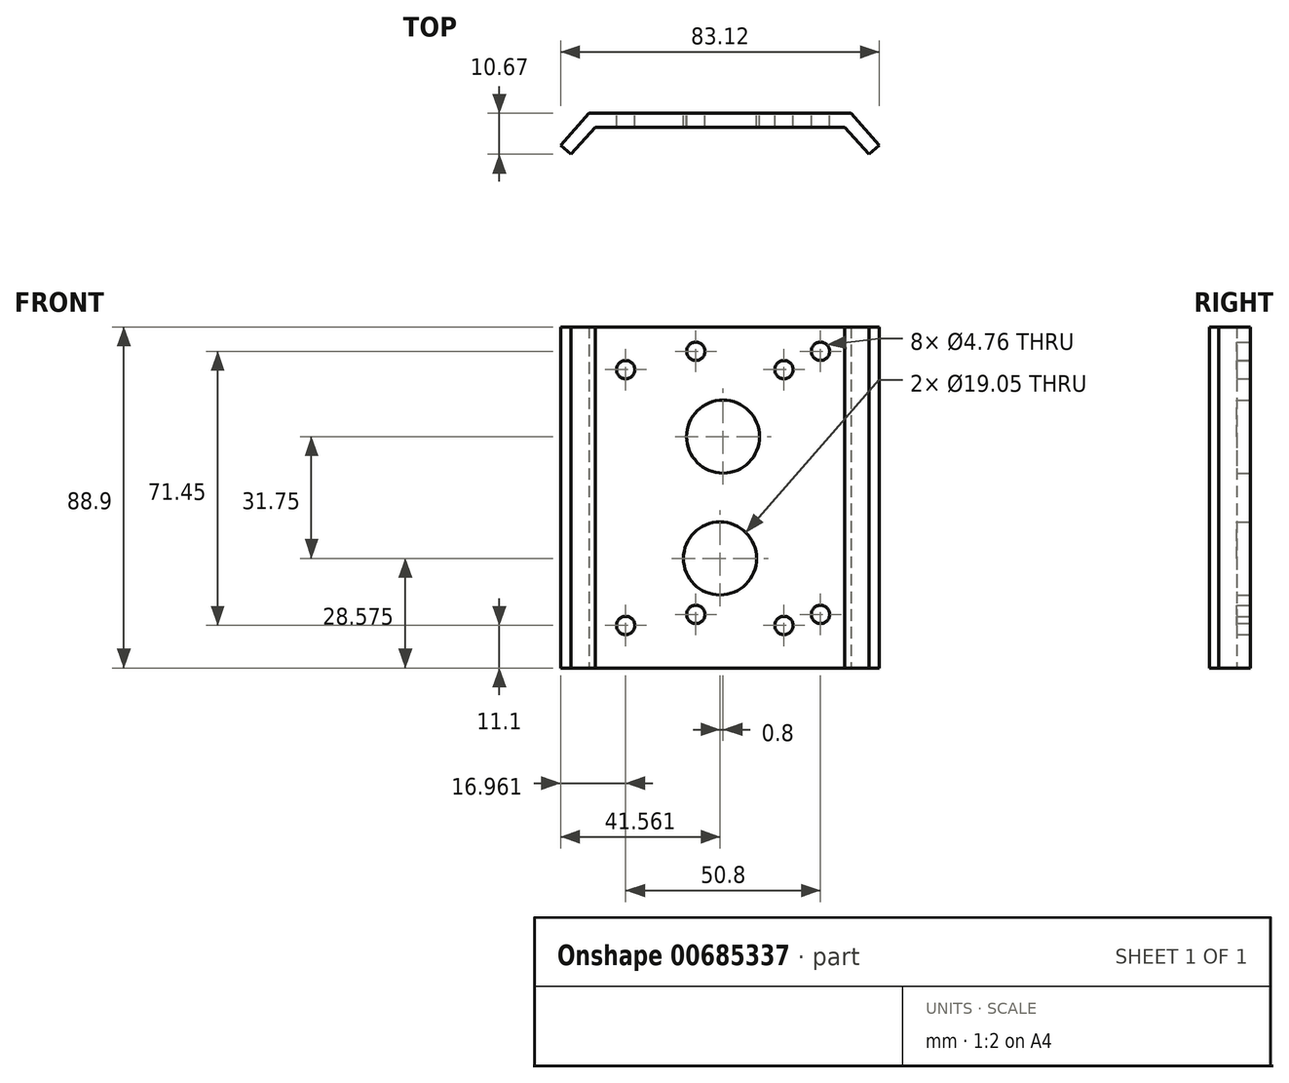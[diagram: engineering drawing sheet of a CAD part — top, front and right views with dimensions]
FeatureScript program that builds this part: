
annotation { "Feature Type Name" : "Feature", "Feature Type Description" : "" }
export const myFeature = defineFeature(function(context is Context, id is Id, definition is map)
    precondition{}
    {
        {
            var Q0;
            Q0=qCreatedBy(makeId("Top.planeOp"),FACE);
            var sketch = newSketch(context, id + "F0", { "sketchPlane" : qUnion([Q0])});
            skLineSegment(sketch, "E0", {"start": v(-57.76, 10.67) * mm, "end": v(10.54, 10.67) * mm});
            skLineSegment(sketch, "E1", {"start": v(10.54, 10.67) * mm, "end": v(17.95, 2.38) * mm});
            skLineSegment(sketch, "E2", {"start": v(15.3, 0) * mm, "end": v(8.94, 7.1) * mm});
            skLineSegment(sketch, "E3", {"start": v(8.94, 7.1) * mm, "end": v(-56.15, 7.1) * mm});
            skLineSegment(sketch, "E4", {"start": v(-56.15, 7.1) * mm, "end": v(-62.5, 0) * mm});
            skLineSegment(sketch, "E5", {"start": v(15.3, 0) * mm, "end": v(17.95, 2.38) * mm});
            skLineSegment(sketch, "E6", {"start": v(-62.5, 0) * mm, "end": v(-65.17, 2.39) * mm});
            skLineSegment(sketch, "E7", {"start": v(-65.17, 2.39) * mm, "end": v(-57.76, 10.67) * mm});
            skLineSegment(sketch, "E8", {"start": v(-63.83, 1.2) * mm, "end": v(-52.04, 14.38) * mm, "construction": true});
            skLineSegment(sketch, "E9", {"start": v(16.62, 1.2) * mm, "end": v(-0.57, 20.4) * mm, "construction": true});
            skSolve(sketch);
        }
        {
            var Q0;
            Q0 = qSketchRegion(id + "F0", true);
            extrude(context, id + "F1", {"entities" : qUnion([Q0]), "depth" : 88.9 * mm, "offsetDistance" : 25.4 * mm});
        }
        {
            var Q0;
            Q0=makeQuery(id+"F1.opExtrude","SWEPT_FACE",FACE,{"disambiguationData":[OSD([sQuery(id+"F0.wireOp",EDGE,"E0")])]});
            var sketch = newSketch(context, id + "F2", { "sketchPlane" : qUnion([Q0])});
            skPoint(sketch, "E10", {"position": v(22.8, 60.33) * mm});
            skPoint(sketch, "E11", {"position": v(23.6, 28.58) * mm});
            skSolve(sketch);
        }
        {
            var Q0;
            Q0=sQuery(id+"F2.wireOp",VERTEX,"E10");
            var Q1;
            Q1=sQuery(id+"F2.wireOp",VERTEX,"E11");
            var Q2;
            Q2=makeQuery(id+"F1.opExtrude","SWEPT_BODY",BODY,{"disambiguationData":[OSD([sQuery(id+"F0.wireOp",EDGE,"E0"),sQuery(id+"F0.wireOp",EDGE,"E1"),sQuery(id+"F0.wireOp",EDGE,"E2"),sQuery(id+"F0.wireOp",EDGE,"E3"),sQuery(id+"F0.wireOp",EDGE,"E4"),sQuery(id+"F0.wireOp",EDGE,"E5"),sQuery(id+"F0.wireOp",EDGE,"E6"),sQuery(id+"F0.wireOp",EDGE,"E7")])]});
            hole(context, id + "F3", {"style" : HoleStyle.SIMPLE, "endStyle" : HoleEndStyle.THROUGH, "holeDiameter" : 19.05 * mm, "majorDiameter" : 6.35 * mm, "isTappedThrough" : true, "tappedDepth" : 12.7 * mm, "tapClearance" : 3, "locations" : qUnion([Q0, Q1]), "scope" : qUnion([Q2])});
        }
        {
            var Q0;
            Q0=makeQuery(id+"F1.opExtrude","SWEPT_FACE",FACE,{"disambiguationData":[OSD([sQuery(id+"F0.wireOp",EDGE,"E0")])]});
            var sketch = newSketch(context, id + "F4", { "sketchPlane" : qUnion([Q0])});
            skLineSegment(sketch, "E12", {"start": v(22.8, 60.33) * mm, "end": v(23.6, 88.9) * mm, "construction": true});
            skLineSegment(sketch, "E13", {"start": v(22.8, 60.33) * mm, "end": v(23.6, 0) * mm, "construction": true});
            skPoint(sketch, "E14", {"position": v(-2.6, 82.55) * mm});
            skPoint(sketch, "E15", {"position": v(-2.6, 13.97) * mm});
            skPoint(sketch, "E16", {"position": v(29.92, 82.55) * mm});
            skPoint(sketch, "E17", {"position": v(29.92, 13.97) * mm});
            skPoint(sketch, "E18", {"position": v(6.93, 77.77) * mm});
            skPoint(sketch, "E19", {"position": v(48.2, 77.77) * mm});
            skPoint(sketch, "E20", {"position": v(48.2, 11.1) * mm});
            skPoint(sketch, "E21", {"position": v(6.93, 11.1) * mm});
            skSolve(sketch);
        }
        {
            var Q0;
            Q0=sQuery(id+"F4.wireOp",VERTEX,"E14");
            var Q1;
            Q1=sQuery(id+"F4.wireOp",VERTEX,"E16");
            var Q2;
            Q2=sQuery(id+"F4.wireOp",VERTEX,"E17");
            var Q3;
            Q3=sQuery(id+"F4.wireOp",VERTEX,"E15");
            var Q4;
            Q4=sQuery(id+"F4.wireOp",VERTEX,"42f246d8-84a4-407b-8d1b-aa9defde0de4");
            var Q5;
            Q5=sQuery(id+"F4.wireOp",VERTEX,"E20");
            var Q6;
            Q6=sQuery(id+"F4.wireOp",VERTEX,"E19");
            var Q7;
            Q7=sQuery(id+"F4.wireOp",VERTEX,"E18");
            var Q8;
            Q8=sQuery(id+"F4.wireOp",VERTEX,"E21");
            var Q9;
            Q9=makeQuery(id+"F1.opExtrude","SWEPT_BODY",BODY,{"disambiguationData":[OSD([sQuery(id+"F0.wireOp",EDGE,"E0"),sQuery(id+"F0.wireOp",EDGE,"E1"),sQuery(id+"F0.wireOp",EDGE,"E2"),sQuery(id+"F0.wireOp",EDGE,"E3"),sQuery(id+"F0.wireOp",EDGE,"E4"),sQuery(id+"F0.wireOp",EDGE,"E5"),sQuery(id+"F0.wireOp",EDGE,"E6"),sQuery(id+"F0.wireOp",EDGE,"E7")])]});
            hole(context, id + "F5", {"style" : HoleStyle.SIMPLE, "endStyle" : HoleEndStyle.THROUGH, "holeDiameter" : 4.76 * mm, "majorDiameter" : 6.35 * mm, "isTappedThrough" : true, "tappedDepth" : 12.7 * mm, "tapClearance" : 3, "locations" : qUnion([Q0, Q1, Q2, Q3, Q4, Q5, Q6, Q7, Q8]), "scope" : qUnion([Q9])});
        }
    });
